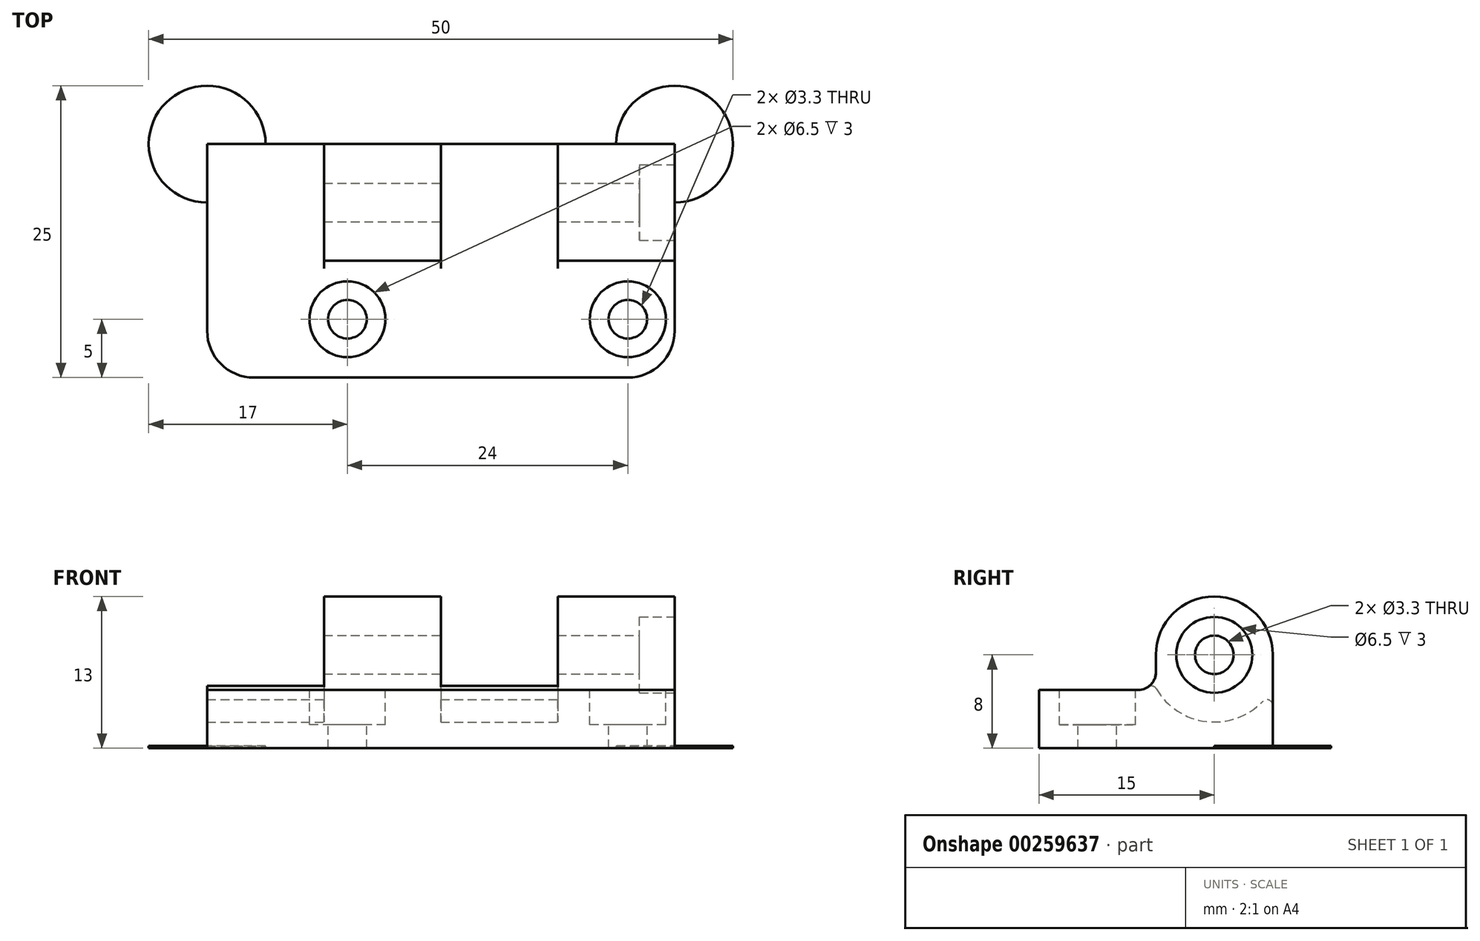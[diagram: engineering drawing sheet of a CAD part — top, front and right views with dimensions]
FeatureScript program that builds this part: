
annotation { "Feature Type Name" : "Feature", "Feature Type Description" : "" }
export const myFeature = defineFeature(function(context is Context, id is Id, definition is map)
    precondition{}
    {
        {
            var Q0;
            Q0=qCreatedBy(makeId("Top.planeOp"),FACE);
            var sketch = newSketch(context, id + "F0", { "sketchPlane" : qUnion([Q0])});
            skLineSegment(sketch, "E0.bottom", {"start": v(4, 0) * mm, "end": v(36, 0) * mm});
            skLineSegment(sketch, "E0.top", {"start": v(0, 14) * mm, "end": v(40, 14) * mm});
            skLineSegment(sketch, "E0.left", {"start": v(0, 4) * mm, "end": v(0, 14) * mm});
            skLineSegment(sketch, "E0.right", {"start": v(40, 4) * mm, "end": v(40, 14) * mm});
            skPoint(sketch, "E1.visualSharp", {"position": v(0, 0) * mm});
            skArc(sketch, "E1.filletArc", {"start": v(0, 4) * mm, "mid": v(1.17, 1.17) * mm, "end": v(4, 0) * mm});
            skPoint(sketch, "E2.visualSharp", {"position": v(40, 0) * mm});
            skArc(sketch, "E2.filletArc", {"start": v(36, 0) * mm, "mid": v(38.83, 1.17) * mm, "end": v(40, 4) * mm});
            skSolve(sketch);
        }
        {
            var Q0;
            Q0 = qSketchRegion(id + "F0", true);
            extrude(context, id + "F1", {"entities" : qUnion([Q0]), "depth" : 5 * mm});
        }
        {
            var Q0;
            Q0=makeQuery(id+"F1.opExtrude","CAP_FACE",FACE,{"disambiguationData":[OSD([sQuery(id+"F0.wireOp",EDGE,"E0.bottom"),sQuery(id+"F0.wireOp",EDGE,"E0.top"),sQuery(id+"F0.wireOp",EDGE,"E0.left"),sQuery(id+"F0.wireOp",EDGE,"E0.right")])],"isStart":false});
            var sketch = newSketch(context, id + "F2", { "sketchPlane" : qUnion([Q0])});
            skLineSegment(sketch, "E3", {"start": v(0, 5) * mm, "end": v(40, 5) * mm, "construction": true});
            skLineSegment(sketch, "E4", {"start": v(20, 5) * mm, "end": v(20, 0) * mm, "construction": true});
            skPoint(sketch, "E5", {"position": v(12, 5) * mm});
            skPoint(sketch, "E6", {"position": v(36, 5) * mm});
            skSolve(sketch);
        }
        {
            var Q0;
            Q0=sQuery(id+"F2.wireOp",VERTEX,"E5");
            var Q1;
            Q1=sQuery(id+"F2.wireOp",VERTEX,"E6");
            var Q2;
            Q2=makeQuery(id+"F1.opExtrude","SWEPT_BODY",BODY,{"disambiguationData":[OSD([sQuery(id+"F0.wireOp",EDGE,"E0.bottom"),sQuery(id+"F0.wireOp",EDGE,"E0.top"),sQuery(id+"F0.wireOp",EDGE,"E0.left"),sQuery(id+"F0.wireOp",EDGE,"E0.right")])]});
            hole(context, id + "F3", {"style" : HoleStyle.C_BORE, "endStyle" : HoleEndStyle.THROUGH, "standardTappedOrClearance" : lookupTablePath({ "standard" : "ISO", "fit" : "Normal", "size" : "M3", "type" : "Clearance" }), "standardBlindInLast" : lookupTablePath({ "fit" : "Standard", "standard" : "ISO", "size" : "M3", "type" : "Clearance" }), "holeDiameter" : 3.3 * mm, "cBoreDiameter" : 6.5 * mm, "cBoreDepth" : 3 * mm, "tappedDepth" : 5.75 * mm, "tapClearance" : 3, "startFromSketch" : true, "locations" : qUnion([Q0, Q1]), "scope" : qUnion([Q2])});
        }
        {
            var Q0;
            Q0=qCreatedBy(makeId("Right.planeOp"),FACE);
            var sketch = newSketch(context, id + "F4", { "sketchPlane" : qUnion([Q0])});
            skLineSegment(sketch, "E7", {"start": v(0, 0) * mm, "end": v(10, 0) * mm, "construction": true});
            skLineSegment(sketch, "E8", {"start": v(10, 0) * mm, "end": v(10, 8) * mm});
            skLineSegment(sketch, "E9", {"start": v(10, 8) * mm, "end": v(20, 8) * mm, "construction": true});
            skLineSegment(sketch, "E10", {"start": v(20, 8) * mm, "end": v(20, 0) * mm});
            skLineSegment(sketch, "E11", {"start": v(20, 0) * mm, "end": v(10, 0) * mm});
            skArc(sketch, "E12", {"start": v(20, 8) * mm, "mid": v(15, 13) * mm, "end": v(10, 8) * mm});
            skArc(sketch, "E13", {"start": v(10, 8) * mm, "mid": v(15, 3) * mm, "end": v(20, 8) * mm, "construction": true});
            skSolve(sketch);
        }
        {
            var Q0;
            Q0 = qSketchRegion(id + "F4", true);
            extrude(context, id + "F5", {"entities" : qUnion([Q0]), "operationType" : NewBodyOperationType.ADD, "depth" : 40 * mm});
        }
        {
            var Q0;
            Q0=makeQuery(id+"F5.boolean.opBoolean","INTERSECT",EDGE,{"derivedFrom":[makeQuery(id+"F1.opExtrude","CAP_FACE",FACE,{"disambiguationData":[OSD([sQuery(id+"F0.wireOp",EDGE,"E0.bottom"),sQuery(id+"F0.wireOp",EDGE,"E0.top"),sQuery(id+"F0.wireOp",EDGE,"E0.left"),sQuery(id+"F0.wireOp",EDGE,"E0.right"),sQuery(id+"F0.wireOp",EDGE,"E1.filletArc"),sQuery(id+"F0.wireOp",EDGE,"E2.filletArc")])],"isStart":false}),makeQuery(id+"F5.opExtrude","SWEPT_FACE",FACE,{"disambiguationData":[OSD([sQuery(id+"F4.wireOp",EDGE,"E8")])]})]});
            fillet(context, id + "F6", {"entities" : qUnion([Q0]), "radius" : 1.5 * mm, "tangentPropagation" : true, "allowEdgeOverflow" : false});
        }
        {
            var Q0;
            Q0=makeQuery(id+"F5.boolean.opBoolean","MERGE",FACE,{"derivedFrom":[makeQuery(id+"F1.opExtrude","SWEPT_FACE",FACE,{"disambiguationData":[OSD([sQuery(id+"F0.wireOp",EDGE,"E0.right")])]}),makeQuery(id+"F5.opExtrude","CAP_FACE",FACE,{"disambiguationData":[OSD([sQuery(id+"F4.wireOp",EDGE,"E8"),sQuery(id+"F4.wireOp",EDGE,"E10"),sQuery(id+"F4.wireOp",EDGE,"E11"),sQuery(id+"F4.wireOp",EDGE,"E12")])],"isStart":false})]});
            var sketch = newSketch(context, id + "F7", { "sketchPlane" : qUnion([Q0])});
            skLineSegment(sketch, "E14", {"start": v(0, 0) * mm, "end": v(15, 0) * mm, "construction": true});
            skLineSegment(sketch, "E15", {"start": v(15, 0) * mm, "end": v(15, 8) * mm, "construction": true});
            skPoint(sketch, "E16", {"position": v(15, 8) * mm});
            skSolve(sketch);
        }
        {
            var Q0;
            Q0=sQuery(id+"F7.wireOp",VERTEX,"E16");
            var Q1;
            Q1=makeQuery(id+"F1.opExtrude","SWEPT_BODY",BODY,{"disambiguationData":[OSD([sQuery(id+"F0.wireOp",EDGE,"E0.bottom"),sQuery(id+"F0.wireOp",EDGE,"E0.top"),sQuery(id+"F0.wireOp",EDGE,"E0.left"),sQuery(id+"F0.wireOp",EDGE,"E0.right"),sQuery(id+"F0.wireOp",EDGE,"E1.filletArc"),sQuery(id+"F0.wireOp",EDGE,"E2.filletArc")])]});
            hole(context, id + "F8", {"style" : HoleStyle.C_BORE, "endStyle" : HoleEndStyle.THROUGH, "standardTappedOrClearance" : lookupTablePath({ "standard" : "ISO", "fit" : "Normal", "size" : "M3", "type" : "Clearance" }), "standardBlindInLast" : lookupTablePath({ "fit" : "Standard", "standard" : "ISO", "size" : "M3", "type" : "Clearance" }), "holeDiameter" : 3.3 * mm, "cBoreDiameter" : 6.5 * mm, "cBoreDepth" : 3 * mm, "tappedDepth" : 5.75 * mm, "tapClearance" : 3, "startFromSketch" : true, "locations" : qUnion([Q0]), "scope" : qUnion([Q1])});
        }
        {
            var Q0;
            Q0=makeQuery(id+"F5.boolean.opBoolean","MERGE",FACE,{"derivedFrom":[makeQuery(id+"F1.opExtrude","SWEPT_FACE",FACE,{"disambiguationData":[OSD([sQuery(id+"F0.wireOp",EDGE,"E0.right")])]}),makeQuery(id+"F5.opExtrude","CAP_FACE",FACE,{"disambiguationData":[OSD([sQuery(id+"F4.wireOp",EDGE,"E8"),sQuery(id+"F4.wireOp",EDGE,"E10"),sQuery(id+"F4.wireOp",EDGE,"E11"),sQuery(id+"F4.wireOp",EDGE,"E12")])],"isStart":false})]});
            cPlane(context, id + "F9", {"entities" : qUnion([Q0]), "cplaneType" : CPlaneType.OFFSET, "offset" : 10 * mm, "oppositeDirection" : true, "width" : 150 * mm, "height" : 150 * mm});
        }
        {
            var Q0;
            Q0=qCreatedBy(id+"F9.planeOp",FACE);
            var sketch = newSketch(context, id + "F10", { "sketchPlane" : qUnion([Q0])});
            skLineSegment(sketch, "E17", {"start": v(0, 0) * mm, "end": v(15, 0) * mm, "construction": true});
            skLineSegment(sketch, "E18", {"start": v(15, 0) * mm, "end": v(15, 8) * mm, "construction": true});
            skCircle(sketch, "E19", {"center": v(15, 8) * mm, "radius": 5.75 * mm});
            skSolve(sketch);
        }
        {
            var Q0;
            Q0 = qSketchRegion(id + "F10", true);
            extrude(context, id + "F11", {"entities" : qUnion([Q0]), "operationType" : NewBodyOperationType.REMOVE, "oppositeDirection" : true, "depth" : 10 * mm});
        }
        {
            var Q0;
            Q0=makeQuery(id+"F5.boolean.opBoolean","MERGE",FACE,{"derivedFrom":[makeQuery(id+"F1.opExtrude","SWEPT_FACE",FACE,{"disambiguationData":[OSD([sQuery(id+"F0.wireOp",EDGE,"E0.right")])]}),makeQuery(id+"F5.opExtrude","CAP_FACE",FACE,{"disambiguationData":[OSD([sQuery(id+"F4.wireOp",EDGE,"E8"),sQuery(id+"F4.wireOp",EDGE,"E10"),sQuery(id+"F4.wireOp",EDGE,"E11"),sQuery(id+"F4.wireOp",EDGE,"E12")])],"isStart":false})]});
            cPlane(context, id + "F12", {"entities" : qUnion([Q0]), "cplaneType" : CPlaneType.OFFSET, "offset" : 30 * mm, "oppositeDirection" : true, "width" : 150 * mm, "height" : 150 * mm});
        }
        {
            var Q0;
            Q0=qCreatedBy(id+"F12.planeOp",FACE);
            var sketch = newSketch(context, id + "F13", { "sketchPlane" : qUnion([Q0])});
            skLineSegment(sketch, "E20", {"start": v(0, 0) * mm, "end": v(15, 0) * mm, "construction": true});
            skLineSegment(sketch, "E21", {"start": v(15, 0) * mm, "end": v(15, 8) * mm, "construction": true});
            skCircle(sketch, "E22", {"center": v(15, 8) * mm, "radius": 5.75 * mm});
            skSolve(sketch);
        }
        {
            var Q0;
            Q0 = qSketchRegion(id + "F13", true);
            extrude(context, id + "F14", {"entities" : qUnion([Q0]), "operationType" : NewBodyOperationType.REMOVE, "endBound" : BoundingType.THROUGH_ALL, "oppositeDirection" : true, "depth" : 25 * mm});
        }
        {
            var Q0;
            Q0=makeQuery(id+"F14.boolean.opBoolean","INTERSECT",EDGE,{"derivedFrom":[makeQuery(id+"F6.opFillet","BLEND_FACE",FACE,{"disambiguationData":[OSD([sQuery(id+"F0.wireOp",EDGE,"E0.bottom"),sQuery(id+"F0.wireOp",EDGE,"E0.top"),sQuery(id+"F0.wireOp",EDGE,"E0.left"),sQuery(id+"F0.wireOp",EDGE,"E0.right"),sQuery(id+"F0.wireOp",EDGE,"E1.filletArc"),sQuery(id+"F0.wireOp",EDGE,"E2.filletArc"),sQuery(id+"F4.wireOp",EDGE,"E8")])]}),makeQuery(id+"F14.opExtrude","SWEPT_FACE",FACE,{"disambiguationData":[OSD([sQuery(id+"F13.wireOp",EDGE,"E22")])]})]});
            var Q1;
            Q1=makeQuery(id+"F14.boolean.opBoolean","INTERSECT",EDGE,{"derivedFrom":[makeQuery(id+"F5.opExtrude","SWEPT_FACE",FACE,{"disambiguationData":[OSD([sQuery(id+"F4.wireOp",EDGE,"E10")])]}),makeQuery(id+"F14.opExtrude","SWEPT_FACE",FACE,{"disambiguationData":[OSD([sQuery(id+"F13.wireOp",EDGE,"E22")])]})]});
            var Q2;
            Q2=makeQuery(id+"F11.boolean.opBoolean","INTERSECT",EDGE,{"derivedFrom":[makeQuery(id+"F5.opExtrude","SWEPT_FACE",FACE,{"disambiguationData":[OSD([sQuery(id+"F4.wireOp",EDGE,"E10")])]}),makeQuery(id+"F11.opExtrude","SWEPT_FACE",FACE,{"disambiguationData":[OSD([sQuery(id+"F10.wireOp",EDGE,"E19")])]})]});
            var Q3;
            Q3=makeQuery(id+"F11.boolean.opBoolean","INTERSECT",EDGE,{"derivedFrom":[makeQuery(id+"F6.opFillet","BLEND_FACE",FACE,{"disambiguationData":[OSD([sQuery(id+"F0.wireOp",EDGE,"E0.bottom"),sQuery(id+"F0.wireOp",EDGE,"E0.top"),sQuery(id+"F0.wireOp",EDGE,"E0.left"),sQuery(id+"F0.wireOp",EDGE,"E0.right"),sQuery(id+"F0.wireOp",EDGE,"E1.filletArc"),sQuery(id+"F0.wireOp",EDGE,"E2.filletArc"),sQuery(id+"F4.wireOp",EDGE,"E8")])]}),makeQuery(id+"F11.opExtrude","SWEPT_FACE",FACE,{"disambiguationData":[OSD([sQuery(id+"F10.wireOp",EDGE,"E19")])]})]});
            fillet(context, id + "F15", {"entities" : qUnion([Q0, Q1, Q2, Q3]), "radius" : 0.5 * mm, "tangentPropagation" : true, "allowEdgeOverflow" : false});
        }
        {
            var Q0;
            Q0=qCreatedBy(makeId("Top.planeOp"),FACE);
            var sketch = newSketch(context, id + "F16", { "sketchPlane" : qUnion([Q0])});
            skLineSegment(sketch, "E23", {"start": v(0, 0) * mm, "end": v(0, 20) * mm, "construction": true});
            skLineSegment(sketch, "E24", {"start": v(0, 0) * mm, "end": v(40, 0) * mm, "construction": true});
            skLineSegment(sketch, "E25", {"start": v(40, 0) * mm, "end": v(40, 20) * mm, "construction": true});
            skCircle(sketch, "E26", {"center": v(0, 20) * mm, "radius": 5 * mm});
            skCircle(sketch, "E27", {"center": v(40, 20) * mm, "radius": 5 * mm});
            skSolve(sketch);
        }
        {
            var Q0;
            Q0 = qSketchRegion(id + "F16", true);
            extrude(context, id + "F17", {"entities" : qUnion([Q0]), "operationType" : NewBodyOperationType.ADD, "depth" : 0.2 * mm});
        }
    });
